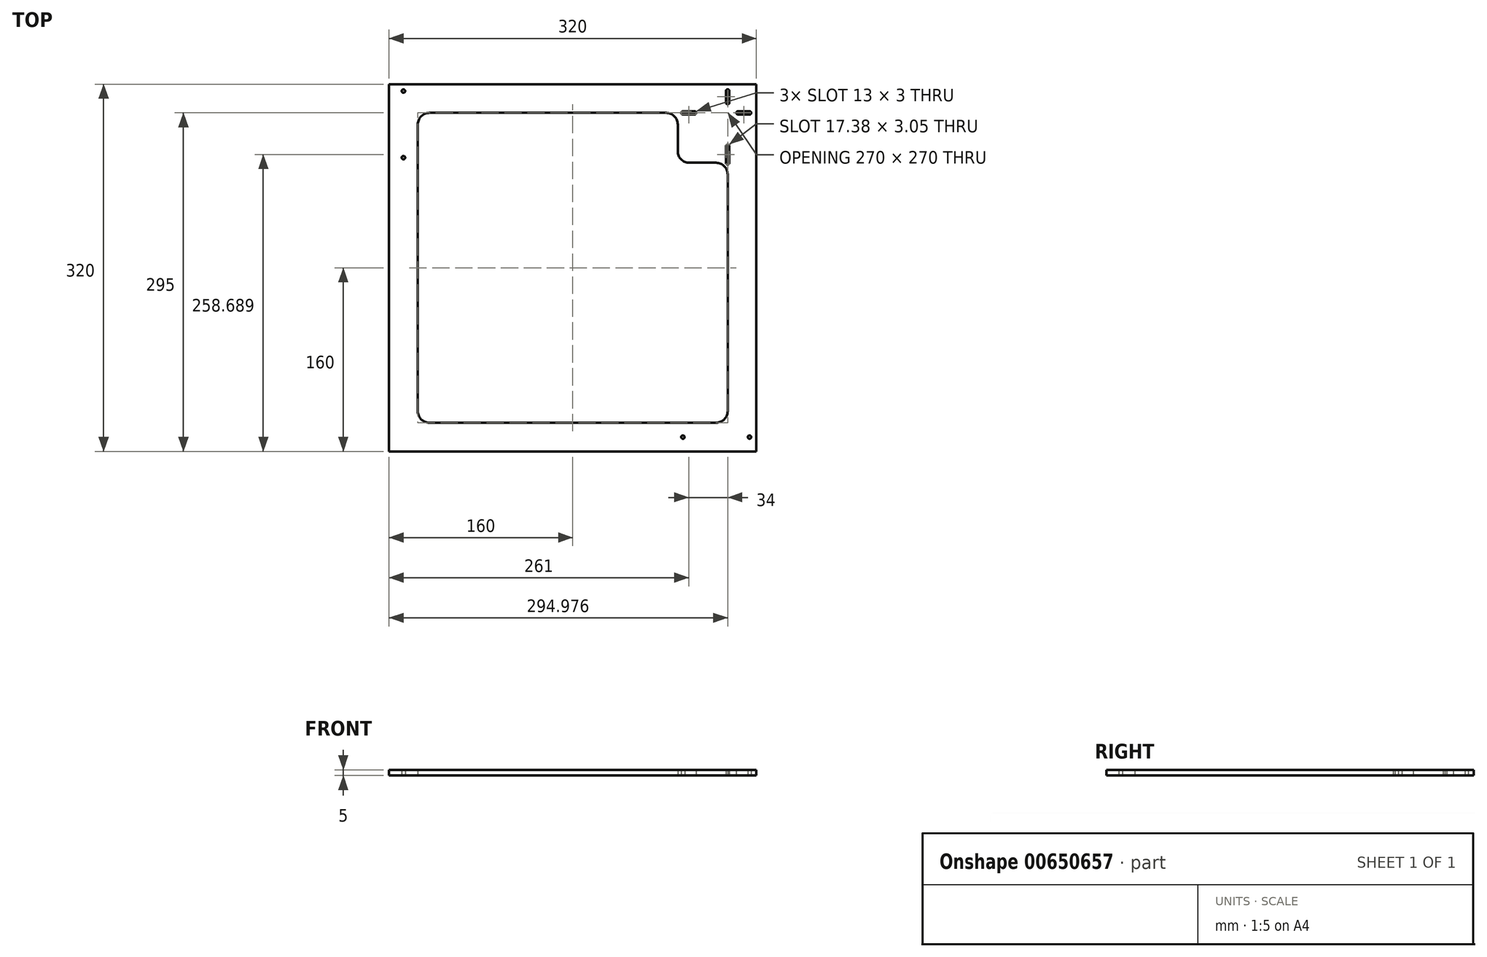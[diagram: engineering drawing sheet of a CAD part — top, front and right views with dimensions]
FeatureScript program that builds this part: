
annotation { "Feature Type Name" : "Feature", "Feature Type Description" : "" }
export const myFeature = defineFeature(function(context is Context, id is Id, definition is map)
    precondition{}
    {
        {
            var Q0;
            Q0=qCreatedBy(makeId("Top.planeOp"),FACE);
            var sketch = newSketch(context, id + "F0", { "sketchPlane" : qUnion([Q0])});
            skLineSegment(sketch, "E0.bottom", {"start": v(160, -160) * mm, "end": v(-160, -160) * mm});
            skLineSegment(sketch, "E0.top", {"start": v(160, 160) * mm, "end": v(-160, 160) * mm});
            skLineSegment(sketch, "E0.left", {"start": v(160, -160) * mm, "end": v(160, 160) * mm});
            skLineSegment(sketch, "E0.right", {"start": v(-160, -160) * mm, "end": v(-160, 160) * mm});
            skPoint(sketch, "E0.middle", {"position": v(0, 0) * mm});
            skLineSegment(sketch, "E1.bottom", {"start": v(125, -135) * mm, "end": v(-125, -135) * mm});
            skLineSegment(sketch, "E1.top", {"start": v(81.5, 135) * mm, "end": v(-125, 135) * mm});
            skLineSegment(sketch, "E1.left", {"start": v(135, -125) * mm, "end": v(135, 81.5) * mm});
            skLineSegment(sketch, "E1.right", {"start": v(-135, -125) * mm, "end": v(-135, 125) * mm});
            skLineSegment(sketch, "E2", {"start": v(-160, 160) * mm, "end": v(-160, 154) * mm, "construction": true});
            skLineSegment(sketch, "E3", {"start": v(-160, 154) * mm, "end": v(-147.5, 154) * mm, "construction": true});
            skLineSegment(sketch, "E4", {"start": v(-147.5, 154) * mm, "end": v(-147.5, 96) * mm, "construction": true});
            skCircle(sketch, "E5", {"center": v(-147.5, 154) * mm, "radius": 1.5 * mm});
            skCircle(sketch, "E6", {"center": v(-147.5, 96) * mm, "radius": 1.5 * mm});
            skLineSegment(sketch, "E7", {"start": v(-160, -160) * mm, "end": v(-160, -147.5) * mm, "construction": true});
            skLineSegment(sketch, "E8", {"start": v(-160, -147.5) * mm, "end": v(-154, -147.5) * mm, "construction": true});
            skLineSegment(sketch, "E9", {"start": v(-154, -147.5) * mm, "end": v(-96, -147.5) * mm, "construction": true});
            skPoint(sketch, "E10.visualSharp", {"position": v(135, 135) * mm});
            skPoint(sketch, "E11.visualSharp", {"position": v(135, -135) * mm});
            skArc(sketch, "E11.filletArc", {"start": v(125, -135) * mm, "mid": v(132.07, -132.07) * mm, "end": v(135, -125) * mm});
            skPoint(sketch, "E12.visualSharp", {"position": v(-135, -135) * mm});
            skArc(sketch, "E12.filletArc", {"start": v(-135, -125) * mm, "mid": v(-132.07, -132.07) * mm, "end": v(-125, -135) * mm});
            skPoint(sketch, "E13.visualSharp", {"position": v(-135, 135) * mm});
            skArc(sketch, "E13.filletArc", {"start": v(-125, 135) * mm, "mid": v(-132.07, 132.07) * mm, "end": v(-135, 125) * mm});
            skLineSegment(sketch, "E14", {"start": v(-147.5, 154) * mm, "end": v(135, 154) * mm, "construction": true});
            skLineSegment(sketch, "E15", {"start": v(136.5, 154) * mm, "end": v(160, 154) * mm, "construction": true});
            skLineSegment(sketch, "E16", {"start": v(160, 154) * mm, "end": v(160, 96) * mm, "construction": true});
            skLineSegment(sketch, "E17", {"start": v(160, 96) * mm, "end": v(135, 95.88) * mm, "construction": true});
            skLineSegment(sketch, "E18", {"start": v(160, -160) * mm, "end": v(160, -147.5) * mm, "construction": true});
            skLineSegment(sketch, "E19", {"start": v(160, -147.5) * mm, "end": v(154, -147.5) * mm, "construction": true});
            skLineSegment(sketch, "E20", {"start": v(154, -147.5) * mm, "end": v(96, -147.5) * mm, "construction": true});
            skCircle(sketch, "E21", {"center": v(96, -147.5) * mm, "radius": 1.5 * mm});
            skCircle(sketch, "E22", {"center": v(154, -147.5) * mm, "radius": 1.5 * mm});
            skLineSegment(sketch, "E23", {"start": v(135, 154) * mm, "end": v(135, 144) * mm, "construction": true});
            skLineSegment(sketch, "E24", {"start": v(160, 160) * mm, "end": v(154, 160) * mm, "construction": true});
            skLineSegment(sketch, "E25", {"start": v(154, 160) * mm, "end": v(154, 136.5) * mm, "construction": true});
            skLineSegment(sketch, "E26", {"start": v(154, 135) * mm, "end": v(144, 135) * mm, "construction": true});
            skArc(sketch, "E27", {"start": v(136.5, 154) * mm, "mid": v(135, 155.5) * mm, "end": v(133.5, 154) * mm});
            skArc(sketch, "E28", {"start": v(133.5, 144) * mm, "mid": v(135, 142.5) * mm, "end": v(136.5, 144) * mm});
            skArc(sketch, "E29", {"start": v(144, 136.5) * mm, "mid": v(142.5, 135) * mm, "end": v(144, 133.5) * mm});
            skArc(sketch, "E30", {"start": v(154, 133.5) * mm, "mid": v(155.5, 135) * mm, "end": v(154, 136.5) * mm});
            skLineSegment(sketch, "E31.bottom", {"start": v(160, 160) * mm, "end": v(110, 160) * mm});
            skLineSegment(sketch, "E31.left", {"start": v(160, 160) * mm, "end": v(160, 110) * mm});
            skLineSegment(sketch, "E32", {"start": v(-147.5, 96) * mm, "end": v(135, 95.88) * mm, "construction": true});
            skLineSegment(sketch, "E33.trimOffspring", {"start": v(91.5, 125) * mm, "end": v(91.5, 101.5) * mm});
            skLineSegment(sketch, "E34.trimOffspring", {"start": v(125, 91.5) * mm, "end": v(101.5, 91.5) * mm});
            skLineSegment(sketch, "E35", {"start": v(96, -147.5) * mm, "end": v(96, 133.5) * mm, "construction": true});
            skLineSegment(sketch, "E36", {"start": v(144, 135) * mm, "end": v(96, 135) * mm, "construction": true});
            skArc(sketch, "E37", {"start": v(96, 136.5) * mm, "mid": v(94.5, 135) * mm, "end": v(96, 133.5) * mm});
            skArc(sketch, "E38", {"start": v(106, 133.5) * mm, "mid": v(107.5, 135) * mm, "end": v(106, 136.5) * mm});
            skPoint(sketch, "E39.visualSharp", {"position": v(91.5, 135) * mm});
            skArc(sketch, "E39.filletArc", {"start": v(91.5, 125) * mm, "mid": v(88.57, 132.07) * mm, "end": v(81.5, 135) * mm});
            skPoint(sketch, "E40.visualSharp", {"position": v(135, 91.5) * mm});
            skArc(sketch, "E40.filletArc", {"start": v(135, 81.5) * mm, "mid": v(132.07, 88.57) * mm, "end": v(125, 91.5) * mm});
            skPoint(sketch, "E41.visualSharp", {"position": v(91.5, 91.5) * mm});
            skArc(sketch, "E41.filletArc", {"start": v(91.5, 101.5) * mm, "mid": v(94.43, 94.43) * mm, "end": v(101.5, 91.5) * mm});
            skArc(sketch, "E42", {"start": v(136.45, 105.88) * mm, "mid": v(134.95, 107.38) * mm, "end": v(133.45, 105.87) * mm});
            skArc(sketch, "E43", {"start": v(133.5, 91.5) * mm, "mid": v(135, 90) * mm, "end": v(136.5, 91.5) * mm});
            skLineSegment(sketch, "E44", {"start": v(136.45, 105.88) * mm, "end": v(136.5, 91.5) * mm});
            skLineSegment(sketch, "E45", {"start": v(106, 133.5) * mm, "end": v(96, 133.5) * mm});
            skLineSegment(sketch, "E46", {"start": v(96, 136.5) * mm, "end": v(106, 136.5) * mm});
            skLineSegment(sketch, "E47", {"start": v(144, 133.5) * mm, "end": v(154, 133.5) * mm});
            skLineSegment(sketch, "E48", {"start": v(154, 135) * mm, "end": v(154, 136.5) * mm});
            skLineSegment(sketch, "E49", {"start": v(154, 136.5) * mm, "end": v(144, 136.5) * mm});
            skLineSegment(sketch, "E50", {"start": v(136.5, 154) * mm, "end": v(136.5, 144) * mm});
            skLineSegment(sketch, "E51", {"start": v(133.5, 144) * mm, "end": v(133.5, 154) * mm});
            skLineSegment(sketch, "E52.trimOffspring", {"start": v(96, 136.5) * mm, "end": v(96, 160) * mm, "construction": true});
            skLineSegment(sketch, "E53", {"start": v(133.5, 91.5) * mm, "end": v(133.45, 105.88) * mm});
            skSolve(sketch);
        }
        {
            var Q0;
            Q0=makeQuery(id+"F0.imprint","IMPRINT",FACE,{"disambiguationData":[TD([[makeQuery(id+"F0.imprint","IMPRINT",EDGE,{"derivedFrom":sQuery(id+"F0.wireOp",EDGE,"E0.bottom")}),-1.0]])]});
            extrude(context, id + "F1", {"entities" : qUnion([Q0]), "depth" : 5 * mm, "offsetDistance" : 25 * mm});
        }
    });
